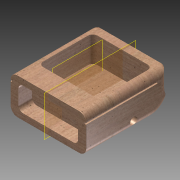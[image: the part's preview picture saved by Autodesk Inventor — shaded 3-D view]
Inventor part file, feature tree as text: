
AUTODESK INVENTOR PART (.ipt)
format: ipt  version: 2015 (Build 190159000, 159)  size: 331,264 bytes
history: native  units: in
note: dims shown in document units (in); Inventor stores cm internally (conversion verified against a paired STEP export)
features: sketch x6, extrude x6, fillet x4, hole x2, plane x2
ambient origin geometry x8: Origin, YZ Plane, XZ Plane, XY Plane, X Axis, Y Axis, Z Axis, Center Point
bodies: Solid1 (feature_tree)
feature tree (20):
  sketch  "Sketch1"  dims[d0=3.17in d1=1.53in]
  extrude  "Extrusion1"  Depth=1.53in
  extrude  "Extrusion5"  Depth=0.2in
  extrude  "Extrusion3"  Depth=1.0in
  extrude  "Extrusion4"  Depth=0.837in
  extrude  "Extrusion6"  Depth=2.5in
  fillet  "Fillet1"  Radius=1.07in
  fillet  "Fillet2"  Radius=0.06in
  fillet  "Fillet3"  Radius=0.3in
  hole  "Hole1"  [1 undecoded]
  hole  "Hole2"  [1 undecoded]
  fillet  "Fillet4"  Radius=0.983in
  plane  "Work Plane1"
  plane  "Work Plane2"
  extrude  "Extrusion7"  Depth=3.0in TaperAngle=0.0deg
  sketch  "Sketch3"  dims[d2=3.5in d3=0.0in d9=0.2in]
  sketch  "Sketch4"  dims[d10=2.5in d11=1.0in]
  sketch  "Sketch5"  dims[d12=0.57in d13=0.0in d15=0.837in]
  sketch  "Sketch6"  dims[d16=2.28in d17=2.5in d18=1.07in d19=0.0in d20=0.06in d21=0.3in]
  sketch  "Sketch9"  dims[d23=3.0in d24=0.0in d25=0.05in d26=0.75in d27=0.983in d28=3.0in d29=0.0in d30=0.75in d31=0.3in d32=0.3in d33=0.1in d34=0.28in d35=0.28in d36=2.8in d37=0.2in d38=0.75in d39=0.375in d40=0.25in d41=0.5635in d42=0.125in d43=0.8108in d44=2.0in d45=0.3in d46=0.305in d47=0.75in d48=0.375in d49=0.25in d50=0.5635in d51=0.35in d52=0.8108in d53=0.01in d54=0.5in d55=-2.0in d56=0.15in d57=0.15in d58=0.3in d59=0.3in d60=0.5in d61=0.0in]
note: 2 required parameter values undecoded (feature->parameter linkage not recoverable at this tier; creation-order binding heuristic only, values carry confidence <= 0.55)
